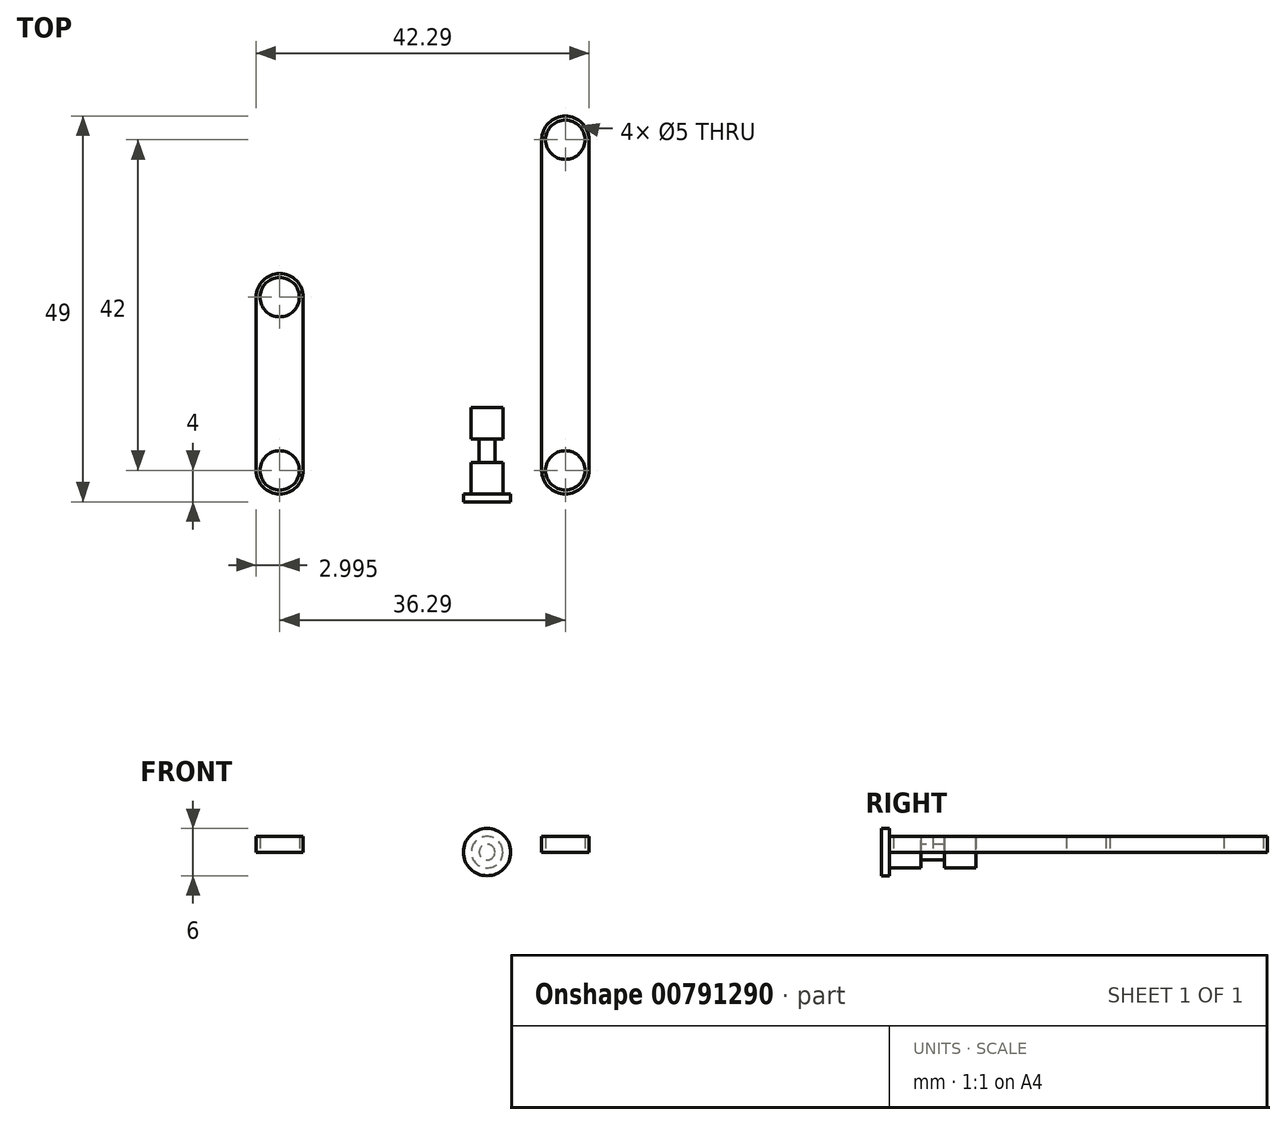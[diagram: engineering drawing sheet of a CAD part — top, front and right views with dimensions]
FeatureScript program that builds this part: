
annotation { "Feature Type Name" : "Feature", "Feature Type Description" : "" }
export const myFeature = defineFeature(function(context is Context, id is Id, definition is map)
    precondition{}
    {
        {
            var Q0;
            Q0=qCreatedBy(makeId("Top.planeOp"),FACE);
            var sketch = newSketch(context, id + "F0", { "sketchPlane" : qUnion([Q0])});
            skLineSegment(sketch, "E0.bottom", {"start": v(-26.34, 0) * mm, "end": v(-26.34, 0) * mm});
            skLineSegment(sketch, "E0.top", {"start": v(-26.34, 28) * mm, "end": v(-26.34, 28) * mm});
            skLineSegment(sketch, "E0.left", {"start": v(-29.34, 3) * mm, "end": v(-29.34, 25) * mm});
            skLineSegment(sketch, "E0.right", {"start": v(-23.34, 3) * mm, "end": v(-23.34, 25) * mm});
            skLineSegment(sketch, "E1", {"start": v(-26.34, 28) * mm, "end": v(-26.34, 0) * mm});
            skCircle(sketch, "E2", {"center": v(-26.34, 3) * mm, "radius": 2.5 * mm});
            skCircle(sketch, "E3", {"center": v(-26.34, 25) * mm, "radius": 2.5 * mm});
            skLineSegment(sketch, "E4.bottom", {"start": v(6.95, 0) * mm, "end": v(9.95, 0) * mm});
            skLineSegment(sketch, "E4.top", {"start": v(9.95, 48) * mm, "end": v(9.95, 48) * mm});
            skLineSegment(sketch, "E4.left", {"start": v(6.95, 0) * mm, "end": v(6.95, 45) * mm});
            skLineSegment(sketch, "E4.right", {"start": v(12.95, 0) * mm, "end": v(12.95, 45) * mm});
            skLineSegment(sketch, "E5", {"start": v(9.95, 48) * mm, "end": v(9.95, 0) * mm});
            skCircle(sketch, "E6", {"center": v(9.95, 3) * mm, "radius": 2.5 * mm});
            skCircle(sketch, "E7", {"center": v(9.95, 45) * mm, "radius": 2.5 * mm});
            skLineSegment(sketch, "E8.bottom", {"start": v(0, 0) * mm, "end": v(-2, 0) * mm});
            skLineSegment(sketch, "E8.top", {"start": v(0, 4) * mm, "end": v(-2, 4) * mm});
            skLineSegment(sketch, "E8.left", {"start": v(0, 0) * mm, "end": v(0, 4) * mm});
            skLineSegment(sketch, "E8.right", {"start": v(-2, 0) * mm, "end": v(-2, 4) * mm});
            skLineSegment(sketch, "E9", {"start": v(6.95, 3) * mm, "end": v(6.95, 3) * mm});
            skLineSegment(sketch, "E10", {"start": v(12.95, 3) * mm, "end": v(12.95, 3) * mm});
            skLineSegment(sketch, "E11", {"start": v(9.95, 0) * mm, "end": v(9.95, 0) * mm});
            skPoint(sketch, "E12.visualSharp", {"position": v(6.95, 0) * mm});
            skArc(sketch, "E12.filletArc", {"start": v(6.95, 3) * mm, "mid": v(7.82, 0.88) * mm, "end": v(9.95, 0) * mm});
            skPoint(sketch, "E13.visualSharp", {"position": v(12.95, 0) * mm});
            skArc(sketch, "E13.filletArc", {"start": v(9.95, 0) * mm, "mid": v(12.07, 0.88) * mm, "end": v(12.95, 3) * mm});
            skPoint(sketch, "E14.visualSharp", {"position": v(6.95, 48) * mm});
            skArc(sketch, "E14.filletArc", {"start": v(9.95, 48) * mm, "mid": v(7.82, 47.12) * mm, "end": v(6.95, 45) * mm});
            skPoint(sketch, "E15.visualSharp", {"position": v(12.95, 48) * mm});
            skArc(sketch, "E15.filletArc", {"start": v(12.95, 45) * mm, "mid": v(12.07, 47.12) * mm, "end": v(9.95, 48) * mm});
            skPoint(sketch, "E16.visualSharp", {"position": v(-29.34, 0) * mm});
            skArc(sketch, "E16.filletArc", {"start": v(-29.34, 3) * mm, "mid": v(-28.47, 0.88) * mm, "end": v(-26.34, 0) * mm});
            skPoint(sketch, "E17.visualSharp", {"position": v(-23.34, 0) * mm});
            skArc(sketch, "E17.filletArc", {"start": v(-26.34, 0) * mm, "mid": v(-24.22, 0.88) * mm, "end": v(-23.34, 3) * mm});
            skPoint(sketch, "E18.visualSharp", {"position": v(-23.34, 28) * mm});
            skArc(sketch, "E18.filletArc", {"start": v(-23.34, 25) * mm, "mid": v(-24.22, 27.12) * mm, "end": v(-26.34, 28) * mm});
            skPoint(sketch, "E19.visualSharp", {"position": v(-29.34, 28) * mm});
            skArc(sketch, "E19.filletArc", {"start": v(-26.34, 28) * mm, "mid": v(-28.47, 27.12) * mm, "end": v(-29.34, 25) * mm});
            skSolve(sketch);
        }
        {
            var Q0;
            {var subQ0=sQuery(id+"F0.wireOp",EDGE,"E0.right");Q0=makeQuery(id+"F0.imprint","IMPRINT",FACE,{"disambiguationData":[TD([[makeQuery(id+"F0.imprint","IMPRINT",EDGE,{"derivedFrom":subQ0}),1.0]])]});}
            var Q1;
            {var subQ5=sQuery(id+"F0.wireOp",EDGE,"E0.left");Q1=makeQuery(id+"F0.imprint","IMPRINT",FACE,{"disambiguationData":[TD([[makeQuery(id+"F0.imprint","IMPRINT",EDGE,{"derivedFrom":subQ5}),-1.0]])]});}
            extrude(context, id + "F1", {"entities" : qUnion([Q0, Q1]), "depth" : 2 * mm, "offsetDistance" : 25 * mm});
        }
        {
            var Q0;
            {var subQ0=sQuery(id+"F0.wireOp",EDGE,"E4.right");Q0=makeQuery(id+"F0.imprint","IMPRINT",FACE,{"disambiguationData":[TD([[makeQuery(id+"F0.imprint","IMPRINT",EDGE,{"derivedFrom":subQ0}),1.0]])]});}
            var Q1;
            {var subQ0=sQuery(id+"F0.wireOp",EDGE,"E12.filletArc");Q1=makeQuery(id+"F0.imprint","IMPRINT",FACE,{"disambiguationData":[TD([[makeQuery(id+"F0.imprint","IMPRINT",EDGE,{"derivedFrom":subQ0}),1.0]])]});}
            extrude(context, id + "F2", {"entities" : qUnion([Q0, Q1]), "depth" : 2 * mm, "offsetDistance" : 25 * mm});
        }
        {
            var Q0;
            Q0=makeQuery(id+"F0.imprint","IMPRINT",FACE,{"disambiguationData":[TD([[makeQuery(id+"F0.imprint","IMPRINT",EDGE,{"derivedFrom":sQuery(id+"F0.wireOp",EDGE,"E8.bottom")}),-1.0]])]});
            var Q1;
            Q1=sQuery(id+"F0.wireOp",EDGE,"E8.left");
            revolve(context, id + "F3", {"surfaceOperationType" : NewSurfaceOperationType.NEW, "entities" : qUnion([Q0]), "axis" : qUnion([Q1]), "revolveType" : RevolveType.FULL});
        }
        {
            var Q0;
            Q0=makeQuery(id+"F3.opRevolve","SWEPT_FACE",FACE,{"disambiguationData":[OSD([sQuery(id+"F0.wireOp",EDGE,"E8.bottom")])]});
            var sketch = newSketch(context, id + "F4", { "sketchPlane" : qUnion([Q0])});
            skCircle(sketch, "E20", {"center": v(0, 0) * mm, "radius": 3 * mm});
            skSolve(sketch);
        }
        {
            var Q0;
            Q0=makeQuery(id+"F4.imprint","IMPRINT",FACE,{"disambiguationData":[TD([[makeQuery(id+"F4.imprint","IMPRINT",EDGE,{"derivedFrom":sQuery(id+"F4.wireOp",EDGE,"E20")}),1.0]])]});
            var Q1;
            Q1=makeQuery(id+"F4.imprint","IMPRINT",FACE,{"disambiguationData":[TD([[makeQuery(id+"F4.imprint","IMPRINT",EDGE,{"derivedFrom":makeQuery(id+"F3.opRevolve","SWEPT_EDGE",EDGE,{"disambiguationData":[OSD([sQuery(id+"F0.wireOp",EDGE,"E8.bottom"),sQuery(id+"F0.wireOp",EDGE,"E8.right")])]})}),1.0]])]});
            extrude(context, id + "F5", {"entities" : qUnion([Q0, Q1]), "operationType" : NewBodyOperationType.ADD, "depth" : 1 * mm, "offsetDistance" : 25 * mm});
        }
        {
            var Q0;
            Q0=makeQuery(id+"F3.opRevolve","SWEPT_FACE",FACE,{"disambiguationData":[OSD([sQuery(id+"F0.wireOp",EDGE,"E8.top")])]});
            var sketch = newSketch(context, id + "F6", { "sketchPlane" : qUnion([Q0])});
            skCircle(sketch, "E21", {"center": v(0, 0) * mm, "radius": 1 * mm});
            skSolve(sketch);
        }
        {
            var Q0;
            Q0=makeQuery(id+"F6.imprint","IMPRINT",FACE,{"disambiguationData":[TD([[makeQuery(id+"F6.imprint","IMPRINT",EDGE,{"derivedFrom":sQuery(id+"F6.wireOp",EDGE,"E21")}),1.0]])]});
            extrude(context, id + "F7", {"entities" : qUnion([Q0]), "operationType" : NewBodyOperationType.ADD, "depth" : 3 * mm, "offsetDistance" : 25 * mm});
        }
        {
            var Q0;
            Q0=makeQuery(id+"F7.opExtrude","CAP_FACE",FACE,{"disambiguationData":[OSD([sQuery(id+"F6.wireOp",EDGE,"E21")])],"isStart":false});
            var sketch = newSketch(context, id + "F8", { "sketchPlane" : qUnion([Q0])});
            skCircle(sketch, "E22", {"center": v(0, 0) * mm, "radius": 2 * mm});
            skSolve(sketch);
        }
        {
            var Q0;
            Q0=makeQuery(id+"F8.imprint","IMPRINT",FACE,{"disambiguationData":[TD([[makeQuery(id+"F8.imprint","IMPRINT",EDGE,{"derivedFrom":sQuery(id+"F8.wireOp",EDGE,"E22")}),1.0]])]});
            var Q1;
            Q1=makeQuery(id+"F8.imprint","IMPRINT",FACE,{"disambiguationData":[TD([[makeQuery(id+"F8.imprint","IMPRINT",EDGE,{"derivedFrom":makeQuery(id+"F7.opExtrude","CAP_EDGE",EDGE,{"disambiguationData":[OSD([sQuery(id+"F6.wireOp",EDGE,"E21")])],"isStart":false})}),1.0]])]});
            extrude(context, id + "F9", {"entities" : qUnion([Q0, Q1]), "operationType" : NewBodyOperationType.ADD, "depth" : 4 * mm, "offsetDistance" : 25 * mm});
        }
    });
